FCSTD DOCUMENT  (FreeCAD 0.21R33771 (Git))
Label: RING2_clean
License: All rights reserved
LicenseURL: http://en.wikipedia.org/wiki/All_rights_reserved
objects: Part::Part2DObjectPython×168, App::FeaturePython×24, App::DocumentObjectGroup×1
note: 168 computed .brp shape members not serialized (recipe doc carries the construction recipe); baked Part::Feature solids carry a one-line shape summary decoded from their .brp

FEATURE [Part::Part2DObjectPython] Rectangle  # Draft 2D object (typed FeaturePython)
  Area = 0
  ChamferSize = 0
  Columns = 1
  FilletRadius = 0
  Height = 6
  Length = 6
  MakeFace = false
  Placement = pos=(268.83,-43.4588,0) rot=(0,0,1;4.81065rad)
  Rows = 1
FEATURE [App::FeaturePython] Text  # WARN: FeaturePython — macro-defined, semantics opaque (R4)
  Placement = pos=(270.79,-53.3517,0) rot=(0,0,-1;4.73892rad)
  Text = 2
FEATURE [App::FeaturePython] Text001  # WARN: FeaturePython — macro-defined, semantics opaque (R4)
  Placement = pos=(268.047,49.5386,0) rot=(0,0,1;2.6241rad)
  Text = 6.
FEATURE [Part::Part2DObjectPython] Circle  # Draft 2D object (typed FeaturePython)
  Area = 1.13097
  FirstAngle = 0
  LastAngle = 0
  MakeFace = true
  Placement = pos=(272.463,-49.7326,0) rot=(0,0,1;4.81065rad)
  Radius = 0.6
FEATURE [Part::Part2DObjectPython] Rectangle001  # Draft 2D object (typed FeaturePython)
  Area = 0
  ChamferSize = 0
  Columns = 1
  FilletRadius = 0
  Height = 6
  Length = 6
  MakeFace = false
  Placement = pos=(270.212,-29.6131,0) rot=(0,0,1;5.20195rad)
  Rows = 1
FEATURE [Part::Part2DObjectPython] Circle001  # Draft 2D object (typed FeaturePython)
  Area = 1.13097
  FirstAngle = 0
  LastAngle = 0
  MakeFace = true
  Placement = pos=(275.963,-34.0271,0) rot=(0,0,1;5.20195rad)
  Radius = 0.6
FEATURE [Part::Part2DObjectPython] Rectangle002  # Draft 2D object (typed FeaturePython)
  Area = 0
  ChamferSize = 0
  Columns = 1
  FilletRadius = 0
  Height = 6
  Length = 6
  MakeFace = false
  Placement = pos=(272.57,-18.45,0) rot=(0,0,1;0rad)
  Rows = 1
FEATURE [Part::Part2DObjectPython] Circle002  # Draft 2D object (typed FeaturePython)
  Area = 1.13097
  FirstAngle = 0
  LastAngle = 0
  MakeFace = true
  Placement = pos=(279.17,-15.45,0) rot=(0,0,1;0rad)
  Radius = 0.6
FEATURE [Part::Part2DObjectPython] Rectangle003  # Draft 2D object (typed FeaturePython)
  Area = 0
  ChamferSize = 0
  Columns = 1
  FilletRadius = 0
  Height = 6
  Length = 6
  MakeFace = false
  Placement = pos=(273,-3,0) rot=(0,0,1;0rad)
  Rows = 1
FEATURE [Part::Part2DObjectPython] Circle003  # Draft 2D object (typed FeaturePython)
  Area = 1.13097
  FirstAngle = 0
  LastAngle = 0
  MakeFace = true
  Placement = pos=(279.6,0,0) rot=(0,0,1;0rad)
  Radius = 0.6
FEATURE [Part::Part2DObjectPython] Rectangle004  # Draft 2D object (typed FeaturePython)
  Area = 0
  ChamferSize = 0
  Columns = 1
  FilletRadius = 0
  Height = 6
  Length = 6
  MakeFace = false
  Placement = pos=(272.573,12.4474,0) rot=(0,0,1;0.000873rad)
  Rows = 1
FEATURE [Part::Part2DObjectPython] Circle004  # Draft 2D object (typed FeaturePython)
  Area = 1.13097
  FirstAngle = 0
  LastAngle = 0
  MakeFace = true
  Placement = pos=(279.17,15.4531,0) rot=(0,0,1;0.000873rad)
  Radius = 0.6
FEATURE [Part::Part2DObjectPython] Rectangle005  # Draft 2D object (typed FeaturePython)
  Area = 0
  ChamferSize = 0
  Columns = 1
  FilletRadius = 0
  Height = 6
  Length = 6
  MakeFace = false
  Placement = pos=(271.516,27.6229,0) rot=(0,0,1;0.078889rad)
  Rows = 1
FEATURE [Part::Part2DObjectPython] Circle005  # Draft 2D object (typed FeaturePython)
  Area = 1.13097
  FirstAngle = 0
  LastAngle = 0
  MakeFace = true
  Placement = pos=(277.859,31.1337,0) rot=(0,0,1;0.078889rad)
  Radius = 0.6
FEATURE [Part::Part2DObjectPython] Rectangle006  # Draft 2D object (typed FeaturePython)
  Area = 0
  ChamferSize = 0
  Columns = 1
  FilletRadius = 0
  Height = 6
  Length = 6
  MakeFace = false
  Placement = pos=(269.11,43.15,0) rot=(0,0,1;0rad)
  Rows = 1
FEATURE [Part::Part2DObjectPython] Circle006  # Draft 2D object (typed FeaturePython)
  Area = 1.13097
  FirstAngle = 0
  LastAngle = 0
  MakeFace = true
  Placement = pos=(275.71,46.15,0) rot=(0,0,1;0rad)
  Radius = 0.6
FEATURE [Part::Part2DObjectPython] Rectangle007  # Draft 2D object (typed FeaturePython)
  Area = 0
  ChamferSize = 0
  Columns = 1
  FilletRadius = 0
  Height = 6
  Length = 6
  MakeFace = false
  Placement = pos=(255.73,93.09,0) rot=(0,0,1;0rad)
  Rows = 1
FEATURE [App::FeaturePython] Text002  # WARN: FeaturePython — macro-defined, semantics opaque (R4)
  Placement = pos=(261.188,89.1931,0) rot=(0,0,-1;4.21532rad)
  Text = 2
FEATURE [App::FeaturePython] Text003  # WARN: FeaturePython — macro-defined, semantics opaque (R4)
  Placement = pos=(207.363,176.926,0) rot=(0,0,1;3.1477rad)
  Text = 7
FEATURE [Part::Part2DObjectPython] Circle007  # Draft 2D object (typed FeaturePython)
  Area = 1.13097
  FirstAngle = 0
  LastAngle = 0
  MakeFace = true
  Placement = pos=(262.33,96.09,0) rot=(0,0,1;0rad)
  Radius = 0.6
FEATURE [Part::Part2DObjectPython] Rectangle008  # Draft 2D object (typed FeaturePython)
  Area = 0
  ChamferSize = 0
  Columns = 1
  FilletRadius = 0
  Height = 6
  Length = 6
  MakeFace = false
  Placement = pos=(252.171,106.249,0) rot=(0,0,1;0.600742rad)
  Rows = 1
FEATURE [Part::Part2DObjectPython] Circle008  # Draft 2D object (typed FeaturePython)
  Area = 1.13097
  FirstAngle = 0
  LastAngle = 0
  MakeFace = true
  Placement = pos=(255.92,112.455,0) rot=(0,0,1;0.600742rad)
  Radius = 0.6
FEATURE [Part::Part2DObjectPython] Rectangle009  # Draft 2D object (typed FeaturePython)
  Area = 0
  ChamferSize = 0
  Columns = 1
  FilletRadius = 0
  Height = 6
  Length = 6
  MakeFace = false
  Placement = pos=(243.371,121.409,0) rot=(0,0,1;0.000175rad)
  Rows = 1
FEATURE [Part::Part2DObjectPython] Circle009  # Draft 2D object (typed FeaturePython)
  Area = 1.13097
  FirstAngle = 0
  LastAngle = 0
  MakeFace = true
  Placement = pos=(249.97,124.411,0) rot=(0,0,1;0.000175rad)
  Radius = 0.6
FEATURE [Part::Part2DObjectPython] Rectangle010  # Draft 2D object (typed FeaturePython)
  Area = 0
  ChamferSize = 0
  Columns = 1
  FilletRadius = 0
  Height = 6
  Length = 6
  MakeFace = false
  Placement = pos=(236.02,135,0) rot=(0,0,1;0rad)
  Rows = 1
FEATURE [Part::Part2DObjectPython] Circle010  # Draft 2D object (typed FeaturePython)
  Area = 1.13097
  FirstAngle = 0
  LastAngle = 0
  MakeFace = true
  Placement = pos=(242.62,138,0) rot=(0,0,1;0rad)
  Radius = 0.6
FEATURE [Part::Part2DObjectPython] Rectangle011  # Draft 2D object (typed FeaturePython)
  Area = 0
  ChamferSize = 0
  Columns = 1
  FilletRadius = 0
  Height = 6
  Length = 6
  MakeFace = false
  Placement = pos=(227.993,154.231,0) rot=(0,0,1;4.6883rad)
  Rows = 1
FEATURE [Part::Part2DObjectPython] Circle011  # Draft 2D object (typed FeaturePython)
  Area = 1.13097
  FirstAngle = 0
  LastAngle = 0
  MakeFace = true
  Placement = pos=(230.833,147.561,0) rot=(0,0,1;4.6883rad)
  Radius = 0.6
FEATURE [Part::Part2DObjectPython] Rectangle012  # Draft 2D object (typed FeaturePython)
  Area = 0
  ChamferSize = 0
  Columns = 1
  FilletRadius = 0
  Height = 6
  Length = 6
  MakeFace = false
  Placement = pos=(219.1,160.85,0) rot=(0,0,1;0rad)
  Rows = 1
FEATURE [Part::Part2DObjectPython] Circle012  # Draft 2D object (typed FeaturePython)
  Area = 1.13097
  FirstAngle = 0
  LastAngle = 0
  MakeFace = true
  Placement = pos=(225.7,163.85,0) rot=(0,0,1;0rad)
  Radius = 0.6
FEATURE [Part::Part2DObjectPython] Rectangle013  # Draft 2D object (typed FeaturePython)
  Area = 0
  ChamferSize = 0
  Columns = 1
  FilletRadius = 0
  Height = 6
  Length = 6
  MakeFace = false
  Placement = pos=(209.58,173.02,0) rot=(0,0,1;0rad)
  Rows = 1
FEATURE [Part::Part2DObjectPython] Circle013  # Draft 2D object (typed FeaturePython)
  Area = 1.13097
  FirstAngle = 0
  LastAngle = 0
  MakeFace = true
  Placement = pos=(216.18,176.02,0) rot=(0,0,1;0rad)
  Radius = 0.6
FEATURE [Part::Part2DObjectPython] Rectangle014  # Draft 2D object (typed FeaturePython)
  Area = 0
  ChamferSize = 0
  Columns = 1
  FilletRadius = 0
  Height = 6
  Length = 6
  MakeFace = false
  Placement = pos=(171.796,212.187,0) rot=(0,0,1;5.59064rad)
  Rows = 1
FEATURE [App::FeaturePython] Text004  # WARN: FeaturePython — macro-defined, semantics opaque (R4)
  Placement = pos=(181.597,207.836,0) rot=(0,0,-1;3.69172rad)
  Text = 2
FEATURE [App::FeaturePython] Text005  # WARN: FeaturePython — macro-defined, semantics opaque (R4)
  Placement = pos=(91.1209,256.902,0) rot=(0,0,1;3.6713rad)
  Text = 8
FEATURE [Part::Part2DObjectPython] Circle014  # Draft 2D object (typed FeaturePython)
  Area = 1.13097
  FirstAngle = 0
  LastAngle = 0
  MakeFace = true
  Placement = pos=(178.791,210.281,0) rot=(0,0,1;5.59064rad)
  Radius = 0.6
FEATURE [Part::Part2DObjectPython] Rectangle015  # Draft 2D object (typed FeaturePython)
  Area = 0
  ChamferSize = 0
  Columns = 1
  FilletRadius = 0
  Height = 6
  Length = 6
  MakeFace = false
  Placement = pos=(160.85,219.1,0) rot=(0,0,1;0rad)
  Rows = 1
FEATURE [Part::Part2DObjectPython] Circle015  # Draft 2D object (typed FeaturePython)
  Area = 1.13097
  FirstAngle = 0
  LastAngle = 0
  MakeFace = true
  Placement = pos=(167.45,222.1,0) rot=(0,0,1;0rad)
  Radius = 0.6
FEATURE [Part::Part2DObjectPython] Rectangle016  # Draft 2D object (typed FeaturePython)
  Area = 0
  ChamferSize = 0
  Columns = 1
  FilletRadius = 0
  Height = 6
  Length = 6
  MakeFace = false
  Placement = pos=(147.37,229.012,0) rot=(0,0,1;5.96414rad)
  Rows = 1
FEATURE [Part::Part2DObjectPython] Circle016  # Draft 2D object (typed FeaturePython)
  Area = 1.13097
  FirstAngle = 0
  LastAngle = 0
  MakeFace = true
  Placement = pos=(154.578,229.791,0) rot=(0,0,1;5.96414rad)
  Radius = 0.6
FEATURE [Part::Part2DObjectPython] Rectangle017  # Draft 2D object (typed FeaturePython)
  Area = 0
  ChamferSize = 0
  Columns = 1
  FilletRadius = 0
  Height = 6
  Length = 6
  MakeFace = false
  Placement = pos=(135,236.02,0) rot=(0,0,1;0rad)
  Rows = 1
FEATURE [Part::Part2DObjectPython] Circle017  # Draft 2D object (typed FeaturePython)
  Area = 1.13097
  FirstAngle = 0
  LastAngle = 0
  MakeFace = true
  Placement = pos=(141.6,239.02,0) rot=(0,0,1;0rad)
  Radius = 0.6
FEATURE [Part::Part2DObjectPython] Rectangle018  # Draft 2D object (typed FeaturePython)
  Area = 0
  ChamferSize = 0
  Columns = 1
  FilletRadius = 0
  Height = 6
  Length = 6
  MakeFace = false
  Placement = pos=(121.41,243.37,0) rot=(0,0,1;0rad)
  Rows = 1
FEATURE [Part::Part2DObjectPython] Circle018  # Draft 2D object (typed FeaturePython)
  Area = 1.13097
  FirstAngle = 0
  LastAngle = 0
  MakeFace = true
  Placement = pos=(128.01,246.37,0) rot=(0,0,1;0rad)
  Radius = 0.6
FEATURE [Part::Part2DObjectPython] Rectangle019  # Draft 2D object (typed FeaturePython)
  Area = 0
  ChamferSize = 0
  Columns = 1
  FilletRadius = 0
  Height = 6
  Length = 6
  MakeFace = false
  Placement = pos=(108.413,249.212,0) rot=(0,0,1;0.292517rad)
  Rows = 1
FEATURE [Part::Part2DObjectPython] Circle019  # Draft 2D object (typed FeaturePython)
  Area = 1.13097
  FirstAngle = 0
  LastAngle = 0
  MakeFace = true
  Placement = pos=(113.867,253.988,0) rot=(0,0,1;0.292517rad)
  Radius = 0.6
FEATURE [Part::Part2DObjectPython] Rectangle020  # Draft 2D object (typed FeaturePython)
  Area = 0
  ChamferSize = 0
  Columns = 1
  FilletRadius = 0
  Height = 6
  Length = 6
  MakeFace = false
  Placement = pos=(95.007,254.628,0) rot=(0,0,1;0.527264rad)
  Rows = 1
FEATURE [Part::Part2DObjectPython] Circle020  # Draft 2D object (typed FeaturePython)
  Area = 1.13097
  FirstAngle = 0
  LastAngle = 0
  MakeFace = true
  Placement = pos=(99.2011,260.541,0) rot=(0,0,1;0.527264rad)
  Radius = 0.6
FEATURE [Part::Part2DObjectPython] Rectangle021  # Draft 2D object (typed FeaturePython)
  Area = 0
  ChamferSize = 0
  Columns = 1
  FilletRadius = 0
  Height = 6
  Length = 6
  MakeFace = false
  Placement = pos=(43.15,269.11,0) rot=(0,0,1;0rad)
  Rows = 1
FEATURE [App::FeaturePython] Text006  # WARN: FeaturePython — macro-defined, semantics opaque (R4)
  Placement = pos=(53.3517,270.79,0) rot=(0,0,-1;3.16812rad)
  Text = 2
FEATURE [App::FeaturePython] Text007  # WARN: FeaturePython — macro-defined, semantics opaque (R4)
  Placement = pos=(-49.5386,268.047,0) rot=(0,0,1;4.1949rad)
  Text = 9
FEATURE [Part::Part2DObjectPython] Circle021  # Draft 2D object (typed FeaturePython)
  Area = 1.13097
  FirstAngle = 0
  LastAngle = 0
  MakeFace = true
  Placement = pos=(49.75,272.11,0) rot=(0,0,1;0rad)
  Radius = 0.6
FEATURE [Part::Part2DObjectPython] Rectangle022  # Draft 2D object (typed FeaturePython)
  Area = 0
  ChamferSize = 0
  Columns = 1
  FilletRadius = 0
  Height = 6
  Length = 6
  MakeFace = false
  Placement = pos=(34.9215,273.077,0) rot=(0,0,1;2.07118rad)
  Rows = 1
FEATURE [Part::Part2DObjectPython] Circle022  # Draft 2D object (typed FeaturePython)
  Area = 1.13097
  FirstAngle = 0
  LastAngle = 0
  MakeFace = true
  Placement = pos=(29.1228,277.429,0) rot=(0,0,1;2.07118rad)
  Radius = 0.6
FEATURE [Part::Part2DObjectPython] Rectangle023  # Draft 2D object (typed FeaturePython)
  Area = 0
  ChamferSize = 0
  Columns = 1
  FilletRadius = 0
  Height = 6
  Length = 6
  MakeFace = false
  Placement = pos=(19.6505,276.166,0) rot=(0,0,1;2.49722rad)
  Rows = 1
FEATURE [Part::Part2DObjectPython] Circle023  # Draft 2D object (typed FeaturePython)
  Area = 1.13097
  FirstAngle = 0
  LastAngle = 0
  MakeFace = true
  Placement = pos=(12.5719,277.733,0) rot=(0,0,1;2.49722rad)
  Radius = 0.6
FEATURE [Part::Part2DObjectPython] Rectangle024  # Draft 2D object (typed FeaturePython)
  Area = 0
  ChamferSize = 0
  Columns = 1
  FilletRadius = 0
  Height = 6
  Length = 6
  MakeFace = false
  Placement = pos=(3.7239,278.033,0) rot=(0,0,1;2.85588rad)
  Rows = 1
FEATURE [Part::Part2DObjectPython] Circle024  # Draft 2D object (typed FeaturePython)
  Area = 1.13097
  FirstAngle = 0
  LastAngle = 0
  MakeFace = true
  Placement = pos=(-3.45406,277.015,0) rot=(0,0,1;2.85588rad)
  Radius = 0.6
FEATURE [Part::Part2DObjectPython] Rectangle025  # Draft 2D object (typed FeaturePython)
  Area = 0
  ChamferSize = 0
  Columns = 1
  FilletRadius = 0
  Height = 6
  Length = 6
  MakeFace = false
  Placement = pos=(-12.4369,278.557,0) rot=(0,0,1;3.13723rad)
  Rows = 1
FEATURE [Part::Part2DObjectPython] Circle025  # Draft 2D object (typed FeaturePython)
  Area = 1.13097
  FirstAngle = 0
  LastAngle = 0
  MakeFace = true
  Placement = pos=(-19.05,275.586,0) rot=(0,0,1;3.13723rad)
  Radius = 0.6
FEATURE [Part::Part2DObjectPython] Rectangle026  # Draft 2D object (typed FeaturePython)
  Area = 0
  ChamferSize = 0
  Columns = 1
  FilletRadius = 0
  Height = 6
  Length = 6
  MakeFace = false
  Placement = pos=(-28.5492,277.835,0) rot=(0,0,1;3.35383rad)
  Rows = 1
FEATURE [Part::Part2DObjectPython] Circle026  # Draft 2D object (typed FeaturePython)
  Area = 1.13097
  FirstAngle = 0
  LastAngle = 0
  MakeFace = true
  Placement = pos=(-34.3692,273.512,0) rot=(0,0,1;3.35383rad)
  Radius = 0.6
FEATURE [Part::Part2DObjectPython] Rectangle027  # Draft 2D object (typed FeaturePython)
  Area = 0
  ChamferSize = 0
  Columns = 1
  FilletRadius = 0
  Height = 6
  Length = 6
  MakeFace = false
  Placement = pos=(-44.4583,276.001,0) rot=(0,0,1;3.51684rad)
  Rows = 1
FEATURE [Part::Part2DObjectPython] Circle027  # Draft 2D object (typed FeaturePython)
  Area = 1.13097
  FirstAngle = 0
  LastAngle = 0
  MakeFace = true
  Placement = pos=(-49.4995,270.791,0) rot=(0,0,1;3.51684rad)
  Radius = 0.6
FEATURE [Part::Part2DObjectPython] Rectangle028  # Draft 2D object (typed FeaturePython)
  Area = 0
  ChamferSize = 0
  Columns = 1
  FilletRadius = 0
  Height = 6
  Length = 6
  MakeFace = false
  Placement = pos=(-95.0924,262.854,0) rot=(0,0,1;3.68963rad)
  Rows = 1
FEATURE [App::FeaturePython] Text008  # WARN: FeaturePython — macro-defined, semantics opaque (R4)
  Placement = pos=(-89.1931,261.188,0) rot=(0,0,-1;2.64452rad)
  Text = 2
FEATURE [App::FeaturePython] Text009  # WARN: FeaturePython — macro-defined, semantics opaque (R4)
  Placement = pos=(-176.926,207.363,0) rot=(0,0,1;4.7185rad)
  Text = 10
FEATURE [Part::Part2DObjectPython] Circle028  # Draft 2D object (typed FeaturePython)
  Area = 1.13097
  FirstAngle = 0
  LastAngle = 0
  MakeFace = true
  Placement = pos=(-99.1628,256.854,0) rot=(0,0,1;3.68963rad)
  Radius = 0.6
FEATURE [Part::Part2DObjectPython] Rectangle029  # Draft 2D object (typed FeaturePython)
  Area = 0
  ChamferSize = 0
  Columns = 1
  FilletRadius = 0
  Height = 6
  Length = 6
  MakeFace = false
  Placement = pos=(-109.044,256.963,0) rot=(0,0,1;3.59678rad)
  Rows = 1
FEATURE [Part::Part2DObjectPython] Circle029  # Draft 2D object (typed FeaturePython)
  Area = 1.13097
  FirstAngle = 0
  LastAngle = 0
  MakeFace = true
  Placement = pos=(-113.653,251.367,0) rot=(0,0,1;3.59678rad)
  Radius = 0.6
FEATURE [Part::Part2DObjectPython] Rectangle030  # Draft 2D object (typed FeaturePython)
  Area = 0
  ChamferSize = 0
  Columns = 1
  FilletRadius = 0
  Height = 6
  Length = 6
  MakeFace = false
  Placement = pos=(-122.433,250.124,0) rot=(0,0,1;3.44214rad)
  Rows = 1
FEATURE [Part::Part2DObjectPython] Circle030  # Draft 2D object (typed FeaturePython)
  Area = 1.13097
  FirstAngle = 0
  LastAngle = 0
  MakeFace = true
  Placement = pos=(-127.849,245.304,0) rot=(0,0,1;3.44214rad)
  Radius = 0.6
FEATURE [Part::Part2DObjectPython] Rectangle031  # Draft 2D object (typed FeaturePython)
  Area = 0
  ChamferSize = 0
  Columns = 1
  FilletRadius = 0
  Height = 6
  Length = 6
  MakeFace = false
  Placement = pos=(-135.423,242.39,0) rot=(0,0,1;3.27406rad)
  Rows = 1
FEATURE [Part::Part2DObjectPython] Circle031  # Draft 2D object (typed FeaturePython)
  Area = 1.13097
  FirstAngle = 0
  LastAngle = 0
  MakeFace = true
  Placement = pos=(-141.568,238.544,0) rot=(0,0,1;3.27406rad)
  Radius = 0.6
FEATURE [Part::Part2DObjectPython] Rectangle032  # Draft 2D object (typed FeaturePython)
  Area = 0
  ChamferSize = 0
  Columns = 1
  FilletRadius = 0
  Height = 6
  Length = 6
  MakeFace = false
  Placement = pos=(-148.179,233.939,0) rot=(0,0,1;3.14788rad)
  Rows = 1
FEATURE [Part::Part2DObjectPython] Circle032  # Draft 2D object (typed FeaturePython)
  Area = 1.13097
  FirstAngle = 0
  LastAngle = 0
  MakeFace = true
  Placement = pos=(-154.76,230.897,0) rot=(0,0,1;3.14788rad)
  Radius = 0.6
FEATURE [Part::Part2DObjectPython] Rectangle033  # Draft 2D object (typed FeaturePython)
  Area = 0
  ChamferSize = 0
  Columns = 1
  FilletRadius = 0
  Height = 6
  Length = 6
  MakeFace = false
  Placement = pos=(-160.673,224.912,0) rot=(0,0,1;3.08068rad)
  Rows = 1
FEATURE [Part::Part2DObjectPython] Circle033  # Draft 2D object (typed FeaturePython)
  Area = 1.13097
  FirstAngle = 0
  LastAngle = 0
  MakeFace = true
  Placement = pos=(-167.443,222.319,0) rot=(0,0,1;3.08068rad)
  Radius = 0.6
FEATURE [Part::Part2DObjectPython] Rectangle034  # Draft 2D object (typed FeaturePython)
  Area = 0
  ChamferSize = 0
  Columns = 1
  FilletRadius = 0
  Height = 6
  Length = 6
  MakeFace = false
  Placement = pos=(-172.799,215.342,0) rot=(0,0,1;3.06497rad)
  Rows = 1
FEATURE [Part::Part2DObjectPython] Circle034  # Draft 2D object (typed FeaturePython)
  Area = 1.13097
  FirstAngle = 0
  LastAngle = 0
  MakeFace = true
  Placement = pos=(-179.609,212.856,0) rot=(0,0,1;3.06497rad)
  Radius = 0.6
FEATURE [Part::Part2DObjectPython] Rectangle035  # Draft 2D object (typed FeaturePython)
  Area = 0
  ChamferSize = 0
  Columns = 1
  FilletRadius = 0
  Height = 6
  Length = 6
  MakeFace = false
  Placement = pos=(-209.785,179.212,0) rot=(0,0,1;3.20791rad)
  Rows = 1
FEATURE [App::FeaturePython] Text010  # WARN: FeaturePython — macro-defined, semantics opaque (R4)
  Placement = pos=(-207.836,181.597,0) rot=(0,0,-1;2.12092rad)
  Text = 2
FEATURE [App::FeaturePython] Text011  # WARN: FeaturePython — macro-defined, semantics opaque (R4)
  Placement = pos=(-256.902,91.1209,0) rot=(0,0,1;5.2421rad)
  Text = 11
FEATURE [Part::Part2DObjectPython] Circle035  # Draft 2D object (typed FeaturePython)
  Area = 1.13097
  FirstAngle = 0
  LastAngle = 0
  MakeFace = true
  Placement = pos=(-216.172,175.781,0) rot=(0,0,1;3.20791rad)
  Radius = 0.6
FEATURE [Part::Part2DObjectPython] Rectangle036  # Draft 2D object (typed FeaturePython)
  Area = 0
  ChamferSize = 0
  Columns = 1
  FilletRadius = 0
  Height = 6
  Length = 6
  MakeFace = false
  Placement = pos=(-219.525,167.222,0) rot=(0,0,1;3.27476rad)
  Rows = 1
FEATURE [Part::Part2DObjectPython] Circle036  # Draft 2D object (typed FeaturePython)
  Area = 1.13097
  FirstAngle = 0
  LastAngle = 0
  MakeFace = true
  Placement = pos=(-225.668,163.372,0) rot=(0,0,1;3.27476rad)
  Radius = 0.6
FEATURE [Part::Part2DObjectPython] Rectangle037  # Draft 2D object (typed FeaturePython)
  Area = 0
  ChamferSize = 0
  Columns = 1
  FilletRadius = 0
  Height = 6
  Length = 6
  MakeFace = false
  Placement = pos=(-228.578,154.698,0) rot=(0,0,1;3.34231rad)
  Rows = 1
FEATURE [Part::Part2DObjectPython] Circle037  # Draft 2D object (typed FeaturePython)
  Area = 1.13097
  FirstAngle = 0
  LastAngle = 0
  MakeFace = true
  Placement = pos=(-234.448,150.442,0) rot=(0,0,1;3.34231rad)
  Radius = 0.6
FEATURE [Part::Part2DObjectPython] Rectangle038  # Draft 2D object (typed FeaturePython)
  Area = 0
  ChamferSize = 0
  Columns = 1
  FilletRadius = 0
  Height = 6
  Length = 6
  MakeFace = false
  Placement = pos=(-236.906,141.678,0) rot=(0,0,1;3.40531rad)
  Rows = 1
FEATURE [Part::Part2DObjectPython] Circle038  # Draft 2D object (typed FeaturePython)
  Area = 1.13097
  FirstAngle = 0
  LastAngle = 0
  MakeFace = true
  Placement = pos=(-242.496,137.062,0) rot=(0,0,1;3.40531rad)
  Radius = 0.6
FEATURE [Part::Part2DObjectPython] Rectangle039  # Draft 2D object (typed FeaturePython)
  Area = 0
  ChamferSize = 0
  Columns = 1
  FilletRadius = 0
  Height = 6
  Length = 6
  MakeFace = false
  Placement = pos=(-244.449,128.193,0) rot=(0,0,1;3.45697rad)
  Rows = 1
FEATURE [Part::Part2DObjectPython] Circle039  # Draft 2D object (typed FeaturePython)
  Area = 1.13097
  FirstAngle = 0
  LastAngle = 0
  MakeFace = true
  Placement = pos=(-249.792,123.293,0) rot=(0,0,1;3.45697rad)
  Radius = 0.6
FEATURE [Part::Part2DObjectPython] Rectangle040  # Draft 2D object (typed FeaturePython)
  Area = 0
  ChamferSize = 0
  Columns = 1
  FilletRadius = 0
  Height = 6
  Length = 6
  MakeFace = false
  Placement = pos=(-251.152,114.263,0) rot=(0,0,1;3.48944rad)
  Rows = 1
FEATURE [Part::Part2DObjectPython] Circle040  # Draft 2D object (typed FeaturePython)
  Area = 1.13097
  FirstAngle = 0
  LastAngle = 0
  MakeFace = true
  Placement = pos=(-256.334,109.193,0) rot=(0,0,1;3.48944rad)
  Radius = 0.6
FEATURE [Part::Part2DObjectPython] Rectangle041  # Draft 2D object (typed FeaturePython)
  Area = 0
  ChamferSize = 0
  Columns = 1
  FilletRadius = 0
  Height = 6
  Length = 6
  MakeFace = false
  Placement = pos=(-256.938,99.9358,0) rot=(0,0,1;3.49101rad)
  Rows = 1
FEATURE [Part::Part2DObjectPython] Circle041  # Draft 2D object (typed FeaturePython)
  Area = 1.13097
  FirstAngle = 0
  LastAngle = 0
  MakeFace = true
  Placement = pos=(-262.112,94.8575,0) rot=(0,0,1;3.49101rad)
  Radius = 0.6
FEATURE [Part::Part2DObjectPython] Rectangle042  # Draft 2D object (typed FeaturePython)
  Area = 0
  ChamferSize = 0
  Columns = 1
  FilletRadius = 0
  Height = 6
  Length = 6
  MakeFace = false
  Placement = pos=(-269.261,49.294,0) rot=(0,0,1;3.19081rad)
  Rows = 1
FEATURE [App::FeaturePython] Text012  # WARN: FeaturePython — macro-defined, semantics opaque (R4)
  Placement = pos=(-270.79,53.3517,0) rot=(0,0,-1;1.59733rad)
  Text = 2
FEATURE [App::FeaturePython] Text013  # WARN: FeaturePython — macro-defined, semantics opaque (R4)
  Placement = pos=(-268.047,-49.5386,0) rot=(0,0,1;5.7657rad)
  Text = 12
FEATURE [Part::Part2DObjectPython] Circle042  # Draft 2D object (typed FeaturePython)
  Area = 1.13097
  FirstAngle = 0
  LastAngle = 0
  MakeFace = true
  Placement = pos=(-275.706,45.9729,0) rot=(0,0,1;3.19081rad)
  Radius = 0.6
FEATURE [Part::Part2DObjectPython] Rectangle043  # Draft 2D object (typed FeaturePython)
  Area = 0
  ChamferSize = 0
  Columns = 1
  FilletRadius = 0
  Height = 6
  Length = 6
  MakeFace = false
  Placement = pos=(-271.068,33.6329,0) rot=(0,0,1;3.0716rad)
  Rows = 1
FEATURE [Part::Part2DObjectPython] Circle043  # Draft 2D object (typed FeaturePython)
  Area = 1.13097
  FirstAngle = 0
  LastAngle = 0
  MakeFace = true
  Placement = pos=(-277.861,31.1018,0) rot=(0,0,1;3.0716rad)
  Radius = 0.6
FEATURE [Part::Part2DObjectPython] Rectangle044  # Draft 2D object (typed FeaturePython)
  Area = 0
  ChamferSize = 0
  Columns = 1
  FilletRadius = 0
  Height = 6
  Length = 6
  MakeFace = false
  Placement = pos=(-272.53,18.4099,0) rot=(0,0,1;3.12833rad)
  Rows = 1
FEATURE [Part::Part2DObjectPython] Circle044  # Draft 2D object (typed FeaturePython)
  Area = 1.13097
  FirstAngle = 0
  LastAngle = 0
  MakeFace = true
  Placement = pos=(-279.17,15.4978,0) rot=(0,0,1;3.12833rad)
  Radius = 0.6
FEATURE [Part::Part2DObjectPython] Rectangle045  # Draft 2D object (typed FeaturePython)
  Area = 0
  ChamferSize = 0
  Columns = 1
  FilletRadius = 0
  Height = 6
  Length = 6
  MakeFace = false
  Placement = pos=(-278.591,-3.35959,0) rot=(0,0,1;0.128456rad)
  Rows = 1
FEATURE [Part::Part2DObjectPython] Circle045  # Draft 2D object (typed FeaturePython)
  Area = 1.13097
  FirstAngle = 0
  LastAngle = 0
  MakeFace = true
  Placement = pos=(-272.43,0.461172,0) rot=(0,0,1;0.128456rad)
  Radius = 0.6
FEATURE [Part::Part2DObjectPython] Rectangle046  # Draft 2D object (typed FeaturePython)
  Area = 0
  ChamferSize = 0
  Columns = 1
  FilletRadius = 0
  Height = 6
  Length = 6
  MakeFace = false
  Placement = pos=(-278.514,-18.505,0) rot=(0,0,1;0.0185rad)
  Rows = 1
FEATURE [Part::Part2DObjectPython] Circle046  # Draft 2D object (typed FeaturePython)
  Area = 1.13097
  FirstAngle = 0
  LastAngle = 0
  MakeFace = true
  Placement = pos=(-271.971,-15.3834,0) rot=(0,0,1;0.0185rad)
  Radius = 0.6
FEATURE [Part::Part2DObjectPython] Rectangle047  # Draft 2D object (typed FeaturePython)
  Area = 0
  ChamferSize = 0
  Columns = 1
  FilletRadius = 0
  Height = 6
  Length = 6
  MakeFace = false
  Placement = pos=(-277.269,-33.8505,0) rot=(0,0,1;0.000175rad)
  Rows = 1
FEATURE [Part::Part2DObjectPython] Circle047  # Draft 2D object (typed FeaturePython)
  Area = 1.13097
  FirstAngle = 0
  LastAngle = 0
  MakeFace = true
  Placement = pos=(-270.67,-30.8494,0) rot=(0,0,1;0.000175rad)
  Radius = 0.6
FEATURE [Part::Part2DObjectPython] Rectangle048  # Draft 2D object (typed FeaturePython)
  Area = 0
  ChamferSize = 0
  Columns = 1
  FilletRadius = 0
  Height = 6
  Length = 6
  MakeFace = false
  Placement = pos=(-275.109,-49.1505,0) rot=(0,0,1;0.000175rad)
  Rows = 1
FEATURE [Part::Part2DObjectPython] Circle048  # Draft 2D object (typed FeaturePython)
  Area = 1.13097
  FirstAngle = 0
  LastAngle = 0
  MakeFace = true
  Placement = pos=(-268.51,-46.1494,0) rot=(0,0,1;0.000175rad)
  Radius = 0.6
FEATURE [Part::Part2DObjectPython] Rectangle049  # Draft 2D object (typed FeaturePython)
  Area = 0
  ChamferSize = 0
  Columns = 1
  FilletRadius = 0
  Height = 6
  Length = 6
  MakeFace = false
  Placement = pos=(-260.937,-99.7136,0) rot=(0,0,1;0.238412rad)
  Rows = 1
FEATURE [App::FeaturePython] Text014  # WARN: FeaturePython — macro-defined, semantics opaque (R4)
  Placement = pos=(-261.188,-89.1931,0) rot=(0,0,-1;1.07373rad)
  Text = 2
FEATURE [App::FeaturePython] Text015  # WARN: FeaturePython — macro-defined, semantics opaque (R4)
  Placement = pos=(-207.363,-176.926,0) rot=(0,0,-1;6.27708rad)
  Text = 1
FEATURE [Part::Part2DObjectPython] Circle049  # Draft 2D object (typed FeaturePython)
  Area = 1.13097
  FirstAngle = 0
  LastAngle = 0
  MakeFace = true
  Placement = pos=(-255.232,-95.2398,0) rot=(0,0,1;0.238412rad)
  Radius = 0.6
FEATURE [Part::Part2DObjectPython] Rectangle050  # Draft 2D object (typed FeaturePython)
  Area = 0
  ChamferSize = 0
  Columns = 1
  FilletRadius = 0
  Height = 6
  Length = 6
  MakeFace = false
  Placement = pos=(-254.835,-114.221,0) rot=(0,0,1;0.32498rad)
  Rows = 1
FEATURE [Part::Part2DObjectPython] Circle050  # Draft 2D object (typed FeaturePython)
  Area = 1.13097
  FirstAngle = 0
  LastAngle = 0
  MakeFace = true
  Placement = pos=(-249.538,-109.271,0) rot=(0,0,1;0.32498rad)
  Radius = 0.6
FEATURE [Part::Part2DObjectPython] Rectangle051  # Draft 2D object (typed FeaturePython)
  Area = 0
  ChamferSize = 0
  Columns = 1
  FilletRadius = 0
  Height = 6
  Length = 6
  MakeFace = false
  Placement = pos=(-247.924,-128.358,0) rot=(0,0,1;0.410327rad)
  Rows = 1
FEATURE [Part::Part2DObjectPython] Circle051  # Draft 2D object (typed FeaturePython)
  Area = 1.13097
  FirstAngle = 0
  LastAngle = 0
  MakeFace = true
  Placement = pos=(-243.069,-122.974,0) rot=(0,0,1;0.410327rad)
  Radius = 0.6
FEATURE [Part::Part2DObjectPython] Rectangle052  # Draft 2D object (typed FeaturePython)
  Area = 0
  ChamferSize = 0
  Columns = 1
  FilletRadius = 0
  Height = 6
  Length = 6
  MakeFace = false
  Placement = pos=(-240.24,-142.063,0) rot=(0,0,1;0.493754rad)
  Rows = 1
FEATURE [Part::Part2DObjectPython] Circle052  # Draft 2D object (typed FeaturePython)
  Area = 1.13097
  FirstAngle = 0
  LastAngle = 0
  MakeFace = true
  Placement = pos=(-235.85,-136.294,0) rot=(0,0,1;0.493754rad)
  Radius = 0.6
FEATURE [Part::Part2DObjectPython] Rectangle053  # Draft 2D object (typed FeaturePython)
  Area = 0
  ChamferSize = 0
  Columns = 1
  FilletRadius = 0
  Height = 6
  Length = 6
  MakeFace = false
  Placement = pos=(-231.812,-155.308,0) rot=(0,0,1;0.573515rad)
  Rows = 1
FEATURE [Part::Part2DObjectPython] Circle053  # Draft 2D object (typed FeaturePython)
  Area = 1.13097
  FirstAngle = 0
  LastAngle = 0
  MakeFace = true
  Placement = pos=(-227.896,-149.207,0) rot=(0,0,1;0.573515rad)
  Radius = 0.6
FEATURE [Part::Part2DObjectPython] Rectangle054  # Draft 2D object (typed FeaturePython)
  Area = 0
  ChamferSize = 0
  Columns = 1
  FilletRadius = 0
  Height = 6
  Length = 6
  MakeFace = false
  Placement = pos=(-222.687,-168.052,0) rot=(0,0,1;0.646644rad)
  Rows = 1
FEATURE [Part::Part2DObjectPython] Circle054  # Draft 2D object (typed FeaturePython)
  Area = 1.13097
  FirstAngle = 0
  LastAngle = 0
  MakeFace = true
  Placement = pos=(-219.227,-161.681,0) rot=(0,0,1;0.646644rad)
  Radius = 0.6
FEATURE [Part::Part2DObjectPython] Rectangle055  # Draft 2D object (typed FeaturePython)
  Area = 0
  ChamferSize = 0
  Columns = 1
  FilletRadius = 0
  Height = 6
  Length = 6
  MakeFace = false
  Placement = pos=(-212.892,-180.251,0) rot=(0,0,1;0.711745rad)
  Rows = 1
FEATURE [Part::Part2DObjectPython] Circle055  # Draft 2D object (typed FeaturePython)
  Area = 1.13097
  FirstAngle = 0
  LastAngle = 0
  MakeFace = true
  Placement = pos=(-209.854,-173.669,0) rot=(0,0,1;0.711745rad)
  Radius = 0.6
FEATURE [Part::Part2DObjectPython] Rectangle056  # Draft 2D object (typed FeaturePython)
  Area = 0
  ChamferSize = 0
  Columns = 1
  FilletRadius = 0
  Height = 6
  Length = 6
  MakeFace = false
  Placement = pos=(-179.02,-215.58,0) rot=(0,0,1;0rad)
  Rows = 1
FEATURE [App::FeaturePython] Text016  # WARN: FeaturePython — macro-defined, semantics opaque (R4)
  Placement = pos=(-181.597,-207.836,0) rot=(0,0,-1;0.550128rad)
  Text = 2
FEATURE [App::FeaturePython] Text017  # WARN: FeaturePython — macro-defined, semantics opaque (R4)
  Placement = pos=(-91.1209,-256.902,0) rot=(0,0,-1;5.75348rad)
  Text = 2
FEATURE [Part::Part2DObjectPython] Circle056  # Draft 2D object (typed FeaturePython)
  Area = 1.13097
  FirstAngle = 0
  LastAngle = 0
  MakeFace = true
  Placement = pos=(-172.42,-212.58,0) rot=(0,0,1;0rad)
  Radius = 0.6
FEATURE [Part::Part2DObjectPython] Rectangle057  # Draft 2D object (typed FeaturePython)
  Area = 0
  ChamferSize = 0
  Columns = 1
  FilletRadius = 0
  Height = 6
  Length = 6
  MakeFace = false
  Placement = pos=(-166.381,-225.505,0) rot=(0,0,1;0.146259rad)
  Rows = 1
FEATURE [Part::Part2DObjectPython] Circle057  # Draft 2D object (typed FeaturePython)
  Area = 1.13097
  FirstAngle = 0
  LastAngle = 0
  MakeFace = true
  Placement = pos=(-160.288,-221.575,0) rot=(0,0,1;0.146259rad)
  Radius = 0.6
FEATURE [Part::Part2DObjectPython] Rectangle058  # Draft 2D object (typed FeaturePython)
  Area = 0
  ChamferSize = 0
  Columns = 1
  FilletRadius = 0
  Height = 6
  Length = 6
  MakeFace = false
  Placement = pos=(-155.393,-231.213,0) rot=(0,0,1;5.5669rad)
  Rows = 1
FEATURE [Part::Part2DObjectPython] Circle058  # Draft 2D object (typed FeaturePython)
  Area = 1.13097
  FirstAngle = 0
  LastAngle = 0
  MakeFace = true
  Placement = pos=(-148.445,-233.284,0) rot=(0,0,1;5.5669rad)
  Radius = 0.6
FEATURE [Part::Part2DObjectPython] Rectangle059  # Draft 2D object (typed FeaturePython)
  Area = 0
  ChamferSize = 0
  Columns = 1
  FilletRadius = 0
  Height = 6
  Length = 6
  MakeFace = false
  Placement = pos=(-142.129,-238.044,0) rot=(0,0,1;5.26566rad)
  Rows = 1
FEATURE [Part::Part2DObjectPython] Circle059  # Draft 2D object (typed FeaturePython)
  Area = 1.13097
  FirstAngle = 0
  LastAngle = 0
  MakeFace = true
  Placement = pos=(-136.108,-242.083,0) rot=(0,0,1;5.26566rad)
  Radius = 0.6
FEATURE [Part::Part2DObjectPython] Rectangle060  # Draft 2D object (typed FeaturePython)
  Area = 0
  ChamferSize = 0
  Columns = 1
  FilletRadius = 0
  Height = 6
  Length = 6
  MakeFace = false
  Placement = pos=(-128.508,-245.271,0) rot=(0,0,1;5.23581rad)
  Rows = 1
FEATURE [Part::Part2DObjectPython] Circle060  # Draft 2D object (typed FeaturePython)
  Area = 1.13097
  FirstAngle = 0
  LastAngle = 0
  MakeFace = true
  Placement = pos=(-122.611,-249.488,0) rot=(0,0,1;5.23581rad)
  Radius = 0.6
FEATURE [Part::Part2DObjectPython] Rectangle061  # Draft 2D object (typed FeaturePython)
  Area = 0
  ChamferSize = 0
  Columns = 1
  FilletRadius = 0
  Height = 6
  Length = 6
  MakeFace = false
  Placement = pos=(-113.42,-255.95,0) rot=(0,0,1;0rad)
  Rows = 1
FEATURE [Part::Part2DObjectPython] Circle061  # Draft 2D object (typed FeaturePython)
  Area = 1.13097
  FirstAngle = 0
  LastAngle = 0
  MakeFace = true
  Placement = pos=(-106.82,-252.95,0) rot=(0,0,1;0rad)
  Radius = 0.6
FEATURE [Part::Part2DObjectPython] Rectangle062  # Draft 2D object (typed FeaturePython)
  Area = 0
  ChamferSize = 0
  Columns = 1
  FilletRadius = 0
  Height = 6
  Length = 6
  MakeFace = false
  Placement = pos=(-100.314,-258.337,0) rot=(0,0,1;5.40494rad)
  Rows = 1
FEATURE [Part::Part2DObjectPython] Circle062  # Draft 2D object (typed FeaturePython)
  Area = 1.13097
  FirstAngle = 0
  LastAngle = 0
  MakeFace = true
  Placement = pos=(-93.7914,-261.501,0) rot=(0,0,1;5.40494rad)
  Radius = 0.6
FEATURE [Part::Part2DObjectPython] Rectangle063  # Draft 2D object (typed FeaturePython)
  Area = 0
  ChamferSize = 0
  Columns = 1
  FilletRadius = 0
  Height = 6
  Length = 6
  MakeFace = false
  Placement = pos=(-50.0466,-273.788,0) rot=(0,0,1;5.90445rad)
  Rows = 1
FEATURE [App::FeaturePython] Text018  # WARN: FeaturePython — macro-defined, semantics opaque (R4)
  Placement = pos=(-53.3517,-270.79,0) rot=(0,0,1;6.25666rad)
  Text = 2
FEATURE [App::FeaturePython] Text019  # WARN: FeaturePython — macro-defined, semantics opaque (R4)
  Placement = pos=(49.5386,-268.047,0) rot=(0,0,1;1.05331rad)
  Text = 3
FEATURE [Part::Part2DObjectPython] Circle063  # Draft 2D object (typed FeaturePython)
  Area = 1.13097
  FirstAngle = 0
  LastAngle = 0
  MakeFace = true
  Placement = pos=(-42.8051,-273.441,0) rot=(0,0,1;5.90445rad)
  Radius = 0.6
FEATURE [Part::Part2DObjectPython] Rectangle064  # Draft 2D object (typed FeaturePython)
  Area = 0
  ChamferSize = 0
  Columns = 1
  FilletRadius = 0
  Height = 6
  Length = 6
  MakeFace = false
  Placement = pos=(-34.3981,-276.596,0) rot=(0,0,1;6.07811rad)
  Rows = 1
FEATURE [Part::Part2DObjectPython] Circle064  # Draft 2D object (typed FeaturePython)
  Area = 1.13097
  FirstAngle = 0
  LastAngle = 0
  MakeFace = true
  Placement = pos=(-27.3254,-275.003,0) rot=(0,0,1;6.07811rad)
  Radius = 0.6
FEATURE [Part::Part2DObjectPython] Rectangle065  # Draft 2D object (typed FeaturePython)
  Area = 0
  ChamferSize = 0
  Columns = 1
  FilletRadius = 0
  Height = 6
  Length = 6
  MakeFace = false
  Placement = pos=(-18.4421,-278.578,0) rot=(0,0,1;0.002618rad)
  Rows = 1
FEATURE [Part::Part2DObjectPython] Circle065  # Draft 2D object (typed FeaturePython)
  Area = 1.13097
  FirstAngle = 0
  LastAngle = 0
  MakeFace = true
  Placement = pos=(-11.85,-275.561,0) rot=(0,0,1;0.002618rad)
  Radius = 0.6
FEATURE [Part::Part2DObjectPython] Rectangle066  # Draft 2D object (typed FeaturePython)
  Area = 0
  ChamferSize = 0
  Columns = 1
  FilletRadius = 0
  Height = 6
  Length = 6
  MakeFace = false
  Placement = pos=(-3,-279,0) rot=(0,0,1;0rad)
  Rows = 1
FEATURE [Part::Part2DObjectPython] Circle066  # Draft 2D object (typed FeaturePython)
  Area = 1.13097
  FirstAngle = 0
  LastAngle = 0
  MakeFace = true
  Placement = pos=(3.6,-276,0) rot=(0,0,1;0rad)
  Radius = 0.6
FEATURE [Part::Part2DObjectPython] Rectangle067  # Draft 2D object (typed FeaturePython)
  Area = 0
  ChamferSize = 0
  Columns = 1
  FilletRadius = 0
  Height = 6
  Length = 6
  MakeFace = false
  Placement = pos=(13.6335,-279.404,0) rot=(0,0,1;0.342957rad)
  Rows = 1
FEATURE [Part::Part2DObjectPython] Circle067  # Draft 2D object (typed FeaturePython)
  Area = 1.13097
  FirstAngle = 0
  LastAngle = 0
  MakeFace = true
  Placement = pos=(18.8404,-274.359,0) rot=(0,0,1;0.342957rad)
  Radius = 0.6
FEATURE [Part::Part2DObjectPython] Rectangle068  # Draft 2D object (typed FeaturePython)
  Area = 0
  ChamferSize = 0
  Columns = 1
  FilletRadius = 0
  Height = 6
  Length = 6
  MakeFace = false
  Placement = pos=(31.6501,-270.103,0) rot=(0,0,1;3.73727rad)
  Rows = 1
FEATURE [Part::Part2DObjectPython] Circle068  # Draft 2D object (typed FeaturePython)
  Area = 1.13097
  FirstAngle = 0
  LastAngle = 0
  MakeFace = true
  Placement = pos=(27.87,-276.29,0) rot=(0,0,1;3.73727rad)
  Radius = 0.6
FEATURE [Part::Part2DObjectPython] Rectangle069  # Draft 2D object (typed FeaturePython)
  Area = 0
  ChamferSize = 0
  Columns = 1
  FilletRadius = 0
  Height = 6
  Length = 6
  MakeFace = false
  Placement = pos=(46.4629,-267.879,0) rot=(0,0,1;3.85316rad)
  Rows = 1
FEATURE [Part::Part2DObjectPython] Circle069  # Draft 2D object (typed FeaturePython)
  Area = 1.13097
  FirstAngle = 0
  LastAngle = 0
  MakeFace = true
  Placement = pos=(43.4236,-274.461,0) rot=(0,0,1;3.85316rad)
  Radius = 0.6
FEATURE [Part::Part2DObjectPython] Rectangle070  # Draft 2D object (typed FeaturePython)
  Area = 0
  ChamferSize = 0
  Columns = 1
  FilletRadius = 0
  Height = 6
  Length = 6
  MakeFace = false
  Placement = pos=(94.9184,-254.652,0) rot=(0,0,1;4.20677rad)
  Rows = 1
FEATURE [App::FeaturePython] Text020  # WARN: FeaturePython — macro-defined, semantics opaque (R4)
  Placement = pos=(89.1931,-261.188,0) rot=(0,0,-1;5.78612rad)
  Text = 2
FEATURE [App::FeaturePython] Text021  # WARN: FeaturePython — macro-defined, semantics opaque (R4)
  Placement = pos=(176.926,-207.363,0) rot=(0,0,1;1.57691rad)
  Text = 4
FEATURE [Part::Part2DObjectPython] Circle070  # Draft 2D object (typed FeaturePython)
  Area = 1.13097
  FirstAngle = 0
  LastAngle = 0
  MakeFace = true
  Placement = pos=(94.3463,-261.88,0) rot=(0,0,1;4.20677rad)
  Radius = 0.6
FEATURE [Part::Part2DObjectPython] Rectangle071  # Draft 2D object (typed FeaturePython)
  Area = 0
  ChamferSize = 0
  Columns = 1
  FilletRadius = 0
  Height = 6
  Length = 6
  MakeFace = false
  Placement = pos=(113.636,-250.183,0) rot=(0,0,1;3.06654rad)
  Rows = 1
FEATURE [Part::Part2DObjectPython] Circle071  # Draft 2D object (typed FeaturePython)
  Area = 1.13097
  FirstAngle = 0
  LastAngle = 0
  MakeFace = true
  Placement = pos=(106.83,-252.68,0) rot=(0,0,1;3.06654rad)
  Radius = 0.6
FEATURE [Part::Part2DObjectPython] Rectangle072  # Draft 2D object (typed FeaturePython)
  Area = 0
  ChamferSize = 0
  Columns = 1
  FilletRadius = 0
  Height = 6
  Length = 6
  MakeFace = false
  Placement = pos=(128.484,-247.553,0) rot=(0,0,1;2.07363rad)
  Rows = 1
FEATURE [Part::Part2DObjectPython] Circle072  # Draft 2D object (typed FeaturePython)
  Area = 1.13097
  FirstAngle = 0
  LastAngle = 0
  MakeFace = true
  Placement = pos=(122.675,-243.216,0) rot=(0,0,1;2.07363rad)
  Radius = 0.6
FEATURE [Part::Part2DObjectPython] Rectangle073  # Draft 2D object (typed FeaturePython)
  Area = 0
  ChamferSize = 0
  Columns = 1
  FilletRadius = 0
  Height = 6
  Length = 6
  MakeFace = false
  Placement = pos=(142.092,-240.141,0) rot=(0,0,1;2.08881rad)
  Rows = 1
FEATURE [Part::Part2DObjectPython] Circle073  # Draft 2D object (typed FeaturePython)
  Area = 1.13097
  FirstAngle = 0
  LastAngle = 0
  MakeFace = true
  Placement = pos=(136.217,-235.892,0) rot=(0,0,1;2.08881rad)
  Radius = 0.6
FEATURE [Part::Part2DObjectPython] Rectangle074  # Draft 2D object (typed FeaturePython)
  Area = 0
  ChamferSize = 0
  Columns = 1
  FilletRadius = 0
  Height = 6
  Length = 6
  MakeFace = false
  Placement = pos=(155.35,-231.587,0) rot=(0,0,1;2.19842rad)
  Rows = 1
FEATURE [Part::Part2DObjectPython] Circle074  # Draft 2D object (typed FeaturePython)
  Area = 1.13097
  FirstAngle = 0
  LastAngle = 0
  MakeFace = true
  Placement = pos=(149.046,-228.006,0) rot=(0,0,1;2.19842rad)
  Radius = 0.6
FEATURE [Part::Part2DObjectPython] Rectangle075  # Draft 2D object (typed FeaturePython)
  Area = 0
  ChamferSize = 0
  Columns = 1
  FilletRadius = 0
  Height = 6
  Length = 6
  MakeFace = false
  Placement = pos=(168.091,-222.203,0) rot=(0,0,1;2.33193rad)
  Rows = 1
FEATURE [Part::Part2DObjectPython] Circle075  # Draft 2D object (typed FeaturePython)
  Area = 1.13097
  FirstAngle = 0
  LastAngle = 0
  MakeFace = true
  Placement = pos=(161.367,-219.493,0) rot=(0,0,1;2.33193rad)
  Radius = 0.6
FEATURE [Part::Part2DObjectPython] Rectangle076  # Draft 2D object (typed FeaturePython)
  Area = 0
  ChamferSize = 0
  Columns = 1
  FilletRadius = 0
  Height = 6
  Length = 6
  MakeFace = false
  Placement = pos=(180.233,-212.078,0) rot=(0,0,1;2.47488rad)
  Rows = 1
FEATURE [Part::Part2DObjectPython] Circle076  # Draft 2D object (typed FeaturePython)
  Area = 1.13097
  FirstAngle = 0
  LastAngle = 0
  MakeFace = true
  Placement = pos=(173.191,-210.354,0) rot=(0,0,1;2.47488rad)
  Radius = 0.6
FEATURE [Part::Part2DObjectPython] Rectangle077  # Draft 2D object (typed FeaturePython)
  Area = 0
  ChamferSize = 0
  Columns = 1
  FilletRadius = 0
  Height = 6
  Length = 6
  MakeFace = false
  Placement = pos=(216.058,-173.591,0) rot=(0,0,1;2.96584rad)
  Rows = 1
FEATURE [App::FeaturePython] Text022  # WARN: FeaturePython — macro-defined, semantics opaque (R4)
  Placement = pos=(207.836,-181.597,0) rot=(0,0,-1;5.26252rad)
  Text = 2
FEATURE [App::FeaturePython] Text023  # WARN: FeaturePython — macro-defined, semantics opaque (R4)
  Placement = pos=(256.902,-91.1209,0) rot=(0,0,1;2.1005rad)
  Text = 5
FEATURE [Part::Part2DObjectPython] Circle077  # Draft 2D object (typed FeaturePython)
  Area = 1.13097
  FirstAngle = 0
  LastAngle = 0
  MakeFace = true
  Placement = pos=(209.035,-175.391,0) rot=(0,0,1;2.96584rad)
  Radius = 0.6
FEATURE [Part::Part2DObjectPython] Rectangle078  # Draft 2D object (typed FeaturePython)
  Area = 0
  ChamferSize = 0
  Columns = 1
  FilletRadius = 0
  Height = 6
  Length = 6
  MakeFace = false
  Placement = pos=(225.184,-160.936,0) rot=(0,0,1;3.11332rad)
  Rows = 1
FEATURE [Part::Part2DObjectPython] Circle078  # Draft 2D object (typed FeaturePython)
  Area = 1.13097
  FirstAngle = 0
  LastAngle = 0
  MakeFace = true
  Placement = pos=(218.501,-163.748,0) rot=(0,0,1;3.11332rad)
  Radius = 0.6
FEATURE [Part::Part2DObjectPython] Rectangle079  # Draft 2D object (typed FeaturePython)
  Area = 0
  ChamferSize = 0
  Columns = 1
  FilletRadius = 0
  Height = 6
  Length = 6
  MakeFace = false
  Placement = pos=(233.54,-147.823,0) rot=(0,0,1;3.2615rad)
  Rows = 1
FEATURE [Part::Part2DObjectPython] Circle079  # Draft 2D object (typed FeaturePython)
  Area = 1.13097
  FirstAngle = 0
  LastAngle = 0
  MakeFace = true
  Placement = pos=(227.346,-151.591,0) rot=(0,0,1;3.2615rad)
  Radius = 0.6
FEATURE [Part::Part2DObjectPython] Rectangle080  # Draft 2D object (typed FeaturePython)
  Area = 0
  ChamferSize = 0
  Columns = 1
  FilletRadius = 0
  Height = 6
  Length = 6
  MakeFace = false
  Placement = pos=(241.114,-134.31,0) rot=(0,0,1;3.4109rad)
  Rows = 1
FEATURE [Part::Part2DObjectPython] Circle080  # Draft 2D object (typed FeaturePython)
  Area = 1.13097
  FirstAngle = 0
  LastAngle = 0
  MakeFace = true
  Placement = pos=(235.55,-138.958,0) rot=(0,0,1;3.4109rad)
  Radius = 0.6
FEATURE [Part::Part2DObjectPython] Rectangle081  # Draft 2D object (typed FeaturePython)
  Area = 0
  ChamferSize = 0
  Columns = 1
  FilletRadius = 0
  Height = 6
  Length = 6
  MakeFace = false
  Placement = pos=(247.877,-120.444,0) rot=(0,0,1;3.56379rad)
  Rows = 1
FEATURE [Part::Part2DObjectPython] Circle081  # Draft 2D object (typed FeaturePython)
  Area = 1.13097
  FirstAngle = 0
  LastAngle = 0
  MakeFace = true
  Placement = pos=(243.086,-125.885,0) rot=(0,0,1;3.56379rad)
  Radius = 0.6
FEATURE [Part::Part2DObjectPython] Rectangle082  # Draft 2D object (typed FeaturePython)
  Area = 0
  ChamferSize = 0
  Columns = 1
  FilletRadius = 0
  Height = 6
  Length = 6
  MakeFace = false
  Placement = pos=(253.797,-106.263,0) rot=(0,0,1;3.72593rad)
  Rows = 1
FEATURE [Part::Part2DObjectPython] Circle082  # Draft 2D object (typed FeaturePython)
  Area = 1.13097
  FirstAngle = 0
  LastAngle = 0
  MakeFace = true
  Placement = pos=(249.947,-112.406,0) rot=(0,0,1;3.72593rad)
  Radius = 0.6
FEATURE [Part::Part2DObjectPython] Rectangle083  # Draft 2D object (typed FeaturePython)
  Area = 0
  ChamferSize = 0
  Columns = 1
  FilletRadius = 0
  Height = 6
  Length = 6
  MakeFace = false
  Placement = pos=(258.83,-91.8485,0) rot=(0,0,1;3.90343rad)
  Rows = 1
FEATURE [Part::Part2DObjectPython] Circle083  # Draft 2D object (typed FeaturePython)
  Area = 1.13097
  FirstAngle = 0
  LastAngle = 0
  MakeFace = true
  Placement = pos=(256.125,-98.5749,0) rot=(0,0,1;3.90343rad)
  Radius = 0.6
FEATURE [App::DocumentObjectGroup] Everything
  Group = -> [Rectangle,Circle,Rectangle001,Circle001,Rectangle002,Circle002,Rectangle003,Circle003,Rectangle004,Circle004,Rectangle005,Circle005,Rectangle006,Circle006,Rectangle007,Circle007,Rectangle008,Circle008,Rectangle009,Circle009,Rectangle010,Circle010,Rectangle011,Circle011,Rectangle012,Circle012,Rectangle013,Circle013,Rectangle014,Circle014,Rectangle015,Circle015,Rectangle016,Circle016,Rectangle017,+133 more]
